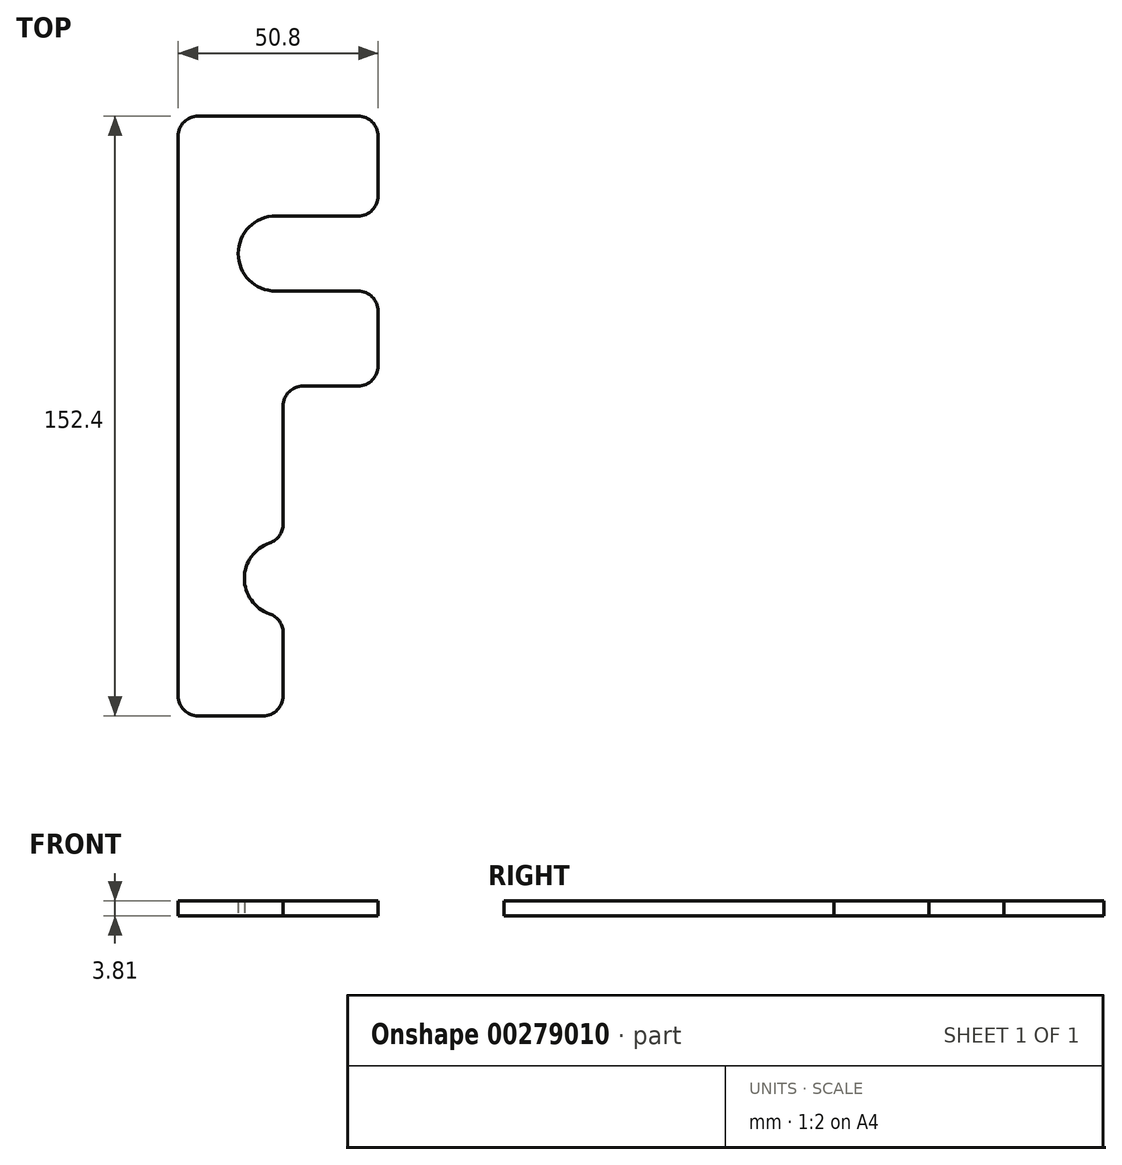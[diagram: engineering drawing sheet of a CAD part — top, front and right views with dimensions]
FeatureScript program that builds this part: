
annotation { "Feature Type Name" : "Feature", "Feature Type Description" : "" }
export const myFeature = defineFeature(function(context is Context, id is Id, definition is map)
    precondition{}
    {
        {
            var Q0;
            Q0=qCreatedBy(makeId("Top.planeOp"),FACE);
            var sketch = newSketch(context, id + "F0", { "sketchPlane" : qUnion([Q0])});
            skLineSegment(sketch, "E0", {"start": v(-32.23, 88.18) * mm, "end": v(-32.23, -64.22) * mm});
            skLineSegment(sketch, "E1", {"start": v(-32.23, -64.22) * mm, "end": v(-5.56, -64.22) * mm});
            skLineSegment(sketch, "E2", {"start": v(-5.56, -64.22) * mm, "end": v(-5.56, -38.82) * mm});
            skLineSegment(sketch, "E3", {"start": v(-5.56, 19.6) * mm, "end": v(18.57, 19.6) * mm});
            skLineSegment(sketch, "E4", {"start": v(18.57, 19.6) * mm, "end": v(18.57, 88.18) * mm});
            skLineSegment(sketch, "E5", {"start": v(18.57, 88.18) * mm, "end": v(-32.23, 88.18) * mm});
            skLineSegment(sketch, "E6.bottom", {"start": v(-7.47, 62.78) * mm, "end": v(10.95, 62.78) * mm, "construction": true});
            skLineSegment(sketch, "E6.top", {"start": v(-7.47, 43.73) * mm, "end": v(10.95, 43.73) * mm, "construction": true});
            skLineSegment(sketch, "E6.left", {"start": v(-17, 53.25) * mm, "end": v(-17, 43.73) * mm, "construction": true});
            skLineSegment(sketch, "E6.right", {"start": v(10.95, 62.78) * mm, "end": v(10.95, 43.73) * mm, "construction": true});
            skLineSegment(sketch, "E7.bottom", {"start": v(-5.9, -19.77) * mm, "end": v(-5.56, -19.77) * mm});
            skLineSegment(sketch, "E7.top", {"start": v(-5.9, -38.82) * mm, "end": v(-5.56, -38.82) * mm});
            skArc(sketch, "E8", {"start": v(-5.9, -19.77) * mm, "mid": v(-15.43, -29.3) * mm, "end": v(-5.9, -38.82) * mm});
            skLineSegment(sketch, "E9.trimOffspring", {"start": v(-5.56, -19.77) * mm, "end": v(-5.56, 19.6) * mm});
            skPoint(sketch, "E10.orphan", {"position": v(10.95, -39.68) * mm});
            skPoint(sketch, "E11.orphan", {"position": v(-17, -19.77) * mm});
            skArc(sketch, "E12", {"start": v(-7.47, 62.78) * mm, "mid": v(-17, 53.25) * mm, "end": v(-7.47, 43.73) * mm});
            skArc(sketch, "E13", {"start": v(1.42, 43.73) * mm, "mid": v(10.95, 53.25) * mm, "end": v(1.42, 62.78) * mm});
            skLineSegment(sketch, "E14", {"start": v(-7.47, 43.73) * mm, "end": v(1.42, 43.73) * mm, "construction": true});
            skLineSegment(sketch, "E15", {"start": v(-7.47, 62.78) * mm, "end": v(1.42, 62.78) * mm});
            skLineSegment(sketch, "E16", {"start": v(-7.47, 43.73) * mm, "end": v(1.42, 43.73) * mm});
            skSolve(sketch);
        }
        {
            var Q0;
            Q0 = qSketchRegion(id + "F0", true);
            extrude(context, id + "F1", {"entities" : qUnion([Q0]), "depth" : 3.8 * mm});
        }
        {
            var Q0;
            Q0=makeQuery(id+"F1.opExtrude","CAP_FACE",FACE,{"disambiguationData":[OSD([sQuery(id+"F0.wireOp",EDGE,"E0"),sQuery(id+"F0.wireOp",EDGE,"E1"),sQuery(id+"F0.wireOp",EDGE,"E2"),sQuery(id+"F0.wireOp",EDGE,"E3"),sQuery(id+"F0.wireOp",EDGE,"E4"),sQuery(id+"F0.wireOp",EDGE,"E5"),sQuery(id+"F0.wireOp",EDGE,"E7.bottom"),sQuery(id+"F0.wireOp",EDGE,"E7.top"),sQuery(id+"F0.wireOp",EDGE,"E8"),sQuery(id+"F0.wireOp",EDGE,"E9.trimOffspring"),sQuery(id+"F0.wireOp",EDGE,"E12"),sQuery(id+"F0.wireOp",EDGE,"E13"),sQuery(id+"F0.wireOp",EDGE,"E15"),sQuery(id+"F0.wireOp",EDGE,"E16")])],"isStart":false});
            var sketch = newSketch(context, id + "F2", { "sketchPlane" : qUnion([Q0])});
            skLineSegment(sketch, "E17.bottom", {"start": v(1.42, 62.78) * mm, "end": v(24.64, 62.78) * mm});
            skLineSegment(sketch, "E17.top", {"start": v(1.42, 43.73) * mm, "end": v(24.64, 43.73) * mm});
            skLineSegment(sketch, "E17.left", {"start": v(1.42, 62.78) * mm, "end": v(1.42, 43.73) * mm});
            skLineSegment(sketch, "E17.right", {"start": v(24.64, 62.78) * mm, "end": v(24.64, 43.73) * mm});
            skSolve(sketch);
        }
        {
            var Q0;
            Q0 = qSketchRegion(id + "F2", true);
            extrude(context, id + "F3", {"entities" : qUnion([Q0]), "operationType" : NewBodyOperationType.REMOVE, "oppositeDirection" : true, "depth" : 25.4 * mm});
        }
        {
            var Q0;
            Q0=makeQuery(id+"F1.opExtrude","SWEPT_EDGE",EDGE,{"disambiguationData":[OSD([sQuery(id+"F0.wireOp",EDGE,"E4"),sQuery(id+"F0.wireOp",EDGE,"E5")])]});
            var Q1;
            Q1=makeQuery(id+"F1.opExtrude","SWEPT_EDGE",EDGE,{"disambiguationData":[OSD([sQuery(id+"F0.wireOp",EDGE,"E0"),sQuery(id+"F0.wireOp",EDGE,"E5")])]});
            var Q2;
            Q2=makeQuery(id+"F1.opExtrude","SWEPT_EDGE",EDGE,{"disambiguationData":[OSD([sQuery(id+"F0.wireOp",EDGE,"E0"),sQuery(id+"F0.wireOp",EDGE,"E1")])]});
            var Q3;
            Q3=makeQuery(id+"F1.opExtrude","SWEPT_EDGE",EDGE,{"disambiguationData":[OSD([sQuery(id+"F0.wireOp",EDGE,"E1"),sQuery(id+"F0.wireOp",EDGE,"E2")])]});
            var Q4;
            Q4=makeQuery(id+"F1.opExtrude","SWEPT_EDGE",EDGE,{"disambiguationData":[OSD([sQuery(id+"F0.wireOp",EDGE,"E7.bottom"),sQuery(id+"F0.wireOp",EDGE,"E9.trimOffspring")])]});
            var Q5;
            Q5=makeQuery(id+"F1.opExtrude","SWEPT_EDGE",EDGE,{"disambiguationData":[OSD([sQuery(id+"F0.wireOp",EDGE,"E2"),sQuery(id+"F0.wireOp",EDGE,"E7.top")])]});
            var Q6;
            Q6=makeQuery(id+"F1.opExtrude","SWEPT_EDGE",EDGE,{"disambiguationData":[OSD([sQuery(id+"F0.wireOp",EDGE,"E3"),sQuery(id+"F0.wireOp",EDGE,"E4")])]});
            var Q7;
            Q7=makeQuery(id+"F1.opExtrude","SWEPT_EDGE",EDGE,{"disambiguationData":[OSD([sQuery(id+"F0.wireOp",EDGE,"E3"),sQuery(id+"F0.wireOp",EDGE,"E9.trimOffspring")])]});
            var Q8;
            Q8=makeQuery(id+"F3.boolean.opBoolean","INTERSECT",EDGE,{"derivedFrom":[makeQuery(id+"F1.opExtrude","SWEPT_FACE",FACE,{"disambiguationData":[OSD([sQuery(id+"F0.wireOp",EDGE,"E4")])]}),makeQuery(id+"F3.opExtrude","SWEPT_FACE",FACE,{"disambiguationData":[OSD([sQuery(id+"F2.wireOp",EDGE,"E17.top")])]})]});
            var Q9;
            Q9=makeQuery(id+"F3.boolean.opBoolean","INTERSECT",EDGE,{"derivedFrom":[makeQuery(id+"F1.opExtrude","SWEPT_FACE",FACE,{"disambiguationData":[OSD([sQuery(id+"F0.wireOp",EDGE,"E4")])]}),makeQuery(id+"F3.opExtrude","SWEPT_FACE",FACE,{"disambiguationData":[OSD([sQuery(id+"F2.wireOp",EDGE,"E17.bottom")])]})]});
            fillet(context, id + "F4", {"entities" : qUnion([Q0, Q1, Q2, Q3, Q4, Q5, Q6, Q7, Q8, Q9]), "radius" : 5.08 * mm, "tangentPropagation" : true, "allowEdgeOverflow" : false});
        }
    });
